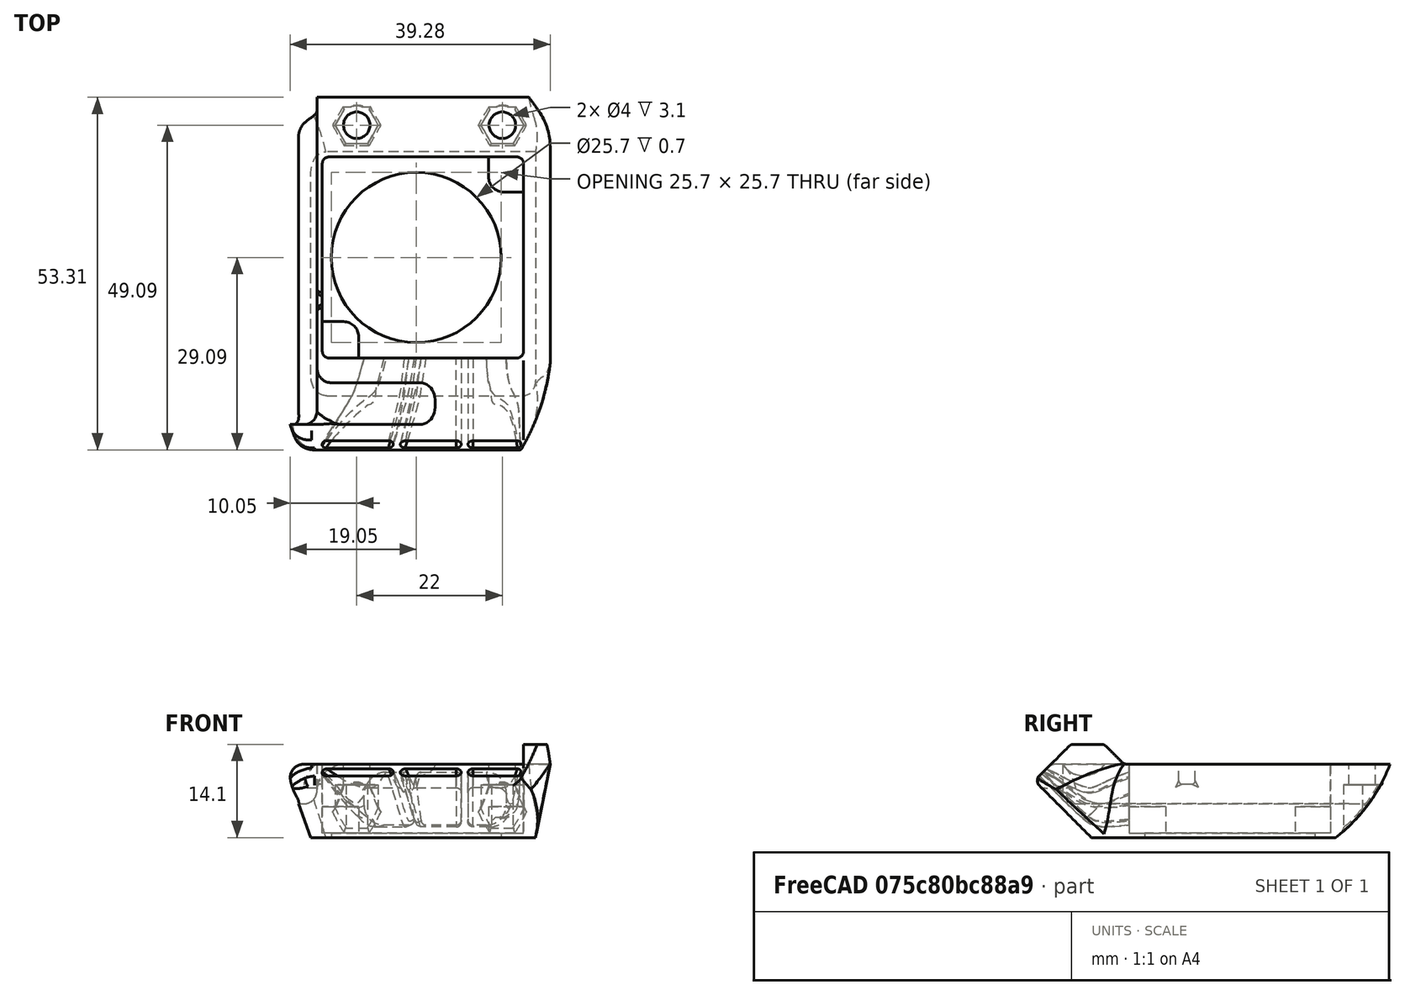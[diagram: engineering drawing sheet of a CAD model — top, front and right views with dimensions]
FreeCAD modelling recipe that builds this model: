
FCSTD DOCUMENT  (FreeCAD 0.18R16146 (Git))
Label: duct
License: Other
LicenseURL: GPL3
objects: Part::Cylinder×4, Part::MultiFuse×3, Part::Feature×1, Part::Chamfer×1, Part::Cut×1
note: 10 computed .brp shape members not serialized (recipe doc carries the construction recipe); baked Part::Feature solids carry a one-line shape summary decoded from their .brp

FEATURE [Part::Feature] Part__Feature152  label="Toolhead_Mosquito"
  Placement = pos=(-5.2,-1,26.5) rot=(0,1,0;4.71239rad)
  shape: bbox 39.62 x 54.74 x 15.9 mm, 125 faces (baked)
FEATURE [Part::Cylinder] Cylinder
  Angle = 360
  AttacherType = Attacher::AttachEngine3D
  Height = 3.1
  Placement = pos=(0.8,28.5,8.1) rot=(0,0,1;0rad)
  Radius = 3
FEATURE [Part::Cylinder] Cylinder001
  Angle = 360
  AttacherType = Attacher::AttachEngine3D
  Height = 3.1
  Placement = pos=(22.8,28.5,8.1) rot=(0,0,1;0rad)
  Radius = 3
FEATURE [Part::Cylinder] Cylinder002
  Angle = 360
  AttacherType = Attacher::AttachEngine3D
  Height = 5
  Placement = pos=(22.8,28.5,8.1) rot=(0,0,1;0rad)
  Radius = 2
FEATURE [Part::Cylinder] Cylinder003
  Angle = 360
  AttacherType = Attacher::AttachEngine3D
  Height = 5
  Placement = pos=(0.8,28.5,8.1) rot=(0,0,1;0rad)
  Radius = 2
FEATURE [Part::MultiFuse] Fusion001
  Placement = pos=(0,0,-0.1) rot=(0,0,1;0rad)
  Shapes = -> [Cylinder,Cylinder001]
FEATURE [Part::Chamfer] Chamfer
  Base = -> Fusion001
  Edges = 2 edges r=0.1: [Edge3,Edge6]
FEATURE [Part::MultiFuse] Fusion
  Placement = pos=(0,0,-0.6) rot=(0,0,1;0rad)
  Shapes = -> [Cylinder002,Cylinder003]
FEATURE [Part::MultiFuse] Fusion002
  Shapes = -> [Chamfer,Part__Feature152]
FEATURE [Part::Cut] Cut
  Base = -> Fusion002
  Tool = -> Fusion
